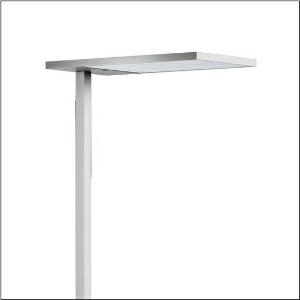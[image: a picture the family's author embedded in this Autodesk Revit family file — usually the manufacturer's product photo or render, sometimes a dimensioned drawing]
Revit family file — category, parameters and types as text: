
# Revit family: silica_r__21_floor_r_51mx53sg4es_3138
name_source: partatom
category: Lighting Fixtures
units: mm (PartAtom-declared; Revit-internal decimal feet)

## family parameters
Cut with Voids When Loaded = No
Host = Face
Light Source = No
Part Type = Normal
Room Calculation Point = No
Round Connector Dimension = Use Diameter
Shared = No

## types (1)
- Silica® 21 Floor R (1 x LED, 15000 lm, 106.4 W, 4000K)
    Apparent Load = 106 VA
    CIE Flux Codes = 54 86 97 13 100
    Color Rendering = 80
    Color Temperature = 4000K
    Default Elevation = 1800 mm
    Description = Silica® 21 Floor R, floorstanding luminaire, of PMMA, primary optical cover: prismatic diffuser, of PMMA, CAT 2 (L<= 3000cd/m²), light emission: indirect/direct distribution, primary light characteristic: symmetric, primary optical cover: cover panel, of PMMA, installation type: not mounted, LED, rated luminous flux: 15.000lm, luminous efficacy: 141lm/W, light colour: 840, colour temperature: 4000K, control gear: DALI 2, daylight-dependent control, mains connection: 230V, AC, 50/60Hz, connection cable included, cable length: 2,5m, rated input power: 106.4W, luminaire head, of aluminium, powder-coated, metallic grey (RAL 9006), length: 671mm, width: 371mm, height: 2010mm, supporting column, angular, of aluminium, powder-coated, metallic grey (RAL 9006), baseplate, of steel, powder-coated, metallic grey (RAL 9006), sensor module PR3-S, local control - self-sufficient standalone sensors, equipment: master, direct and indirect component separately switchable, protection rating (complete): IP20, insulation class (complete): insulation class I (protective earthing), certification: CE, standard: EN 50419, packaging unit: 1 piece
    Height = 18 mm
    Lamp = 1 x LED
    Lamp Light Flux = 15000 lm
    Lamp Power = 106.4 W
    Lamp count = 1
    Length = 650 mm
    Luminous efficacy = 141 lm/W
    Manufacturer = Siteco
    ModVariant = No
    Model = 51MX53SG4ES
    Mounting Place = Floor
    Mounting Type = Freestanding
    Number of Poles = 1
    OnlyDefault = Yes
    Power Factor = 1
    Product Name = Silica® 21 Floor R
    Product group = floorstanding luminaire
    ProductGroupID = 1302
    Protection Class = Protection class I
    Protection Degree = IP 20
    RLX_Detail_Level = 1
    RLX_Emergency_Light_Flux = 0 lm
    RLX_Emergency_Type = 0
    RLX_Emergency_Type_DB = No
    RlxData = <blob elided: 20485 chars, md5=c8c0c493>
    Socket = socket
    Standby Power = 0 W
    System Light Flux = 15000 lm
    System Power = 106 W
    Type Comments = Product without accessories
    Type Image = l_1006716.jpg
    URL = http://relux.com
    VarID = ---
    Voltage = 0 V
    Weight = 0.00 kg
    Width = 350 mm

## geometry (parser evidence)
native form markers: Blend x4, Sweep x17
no freeform markers — native parametric forms only
